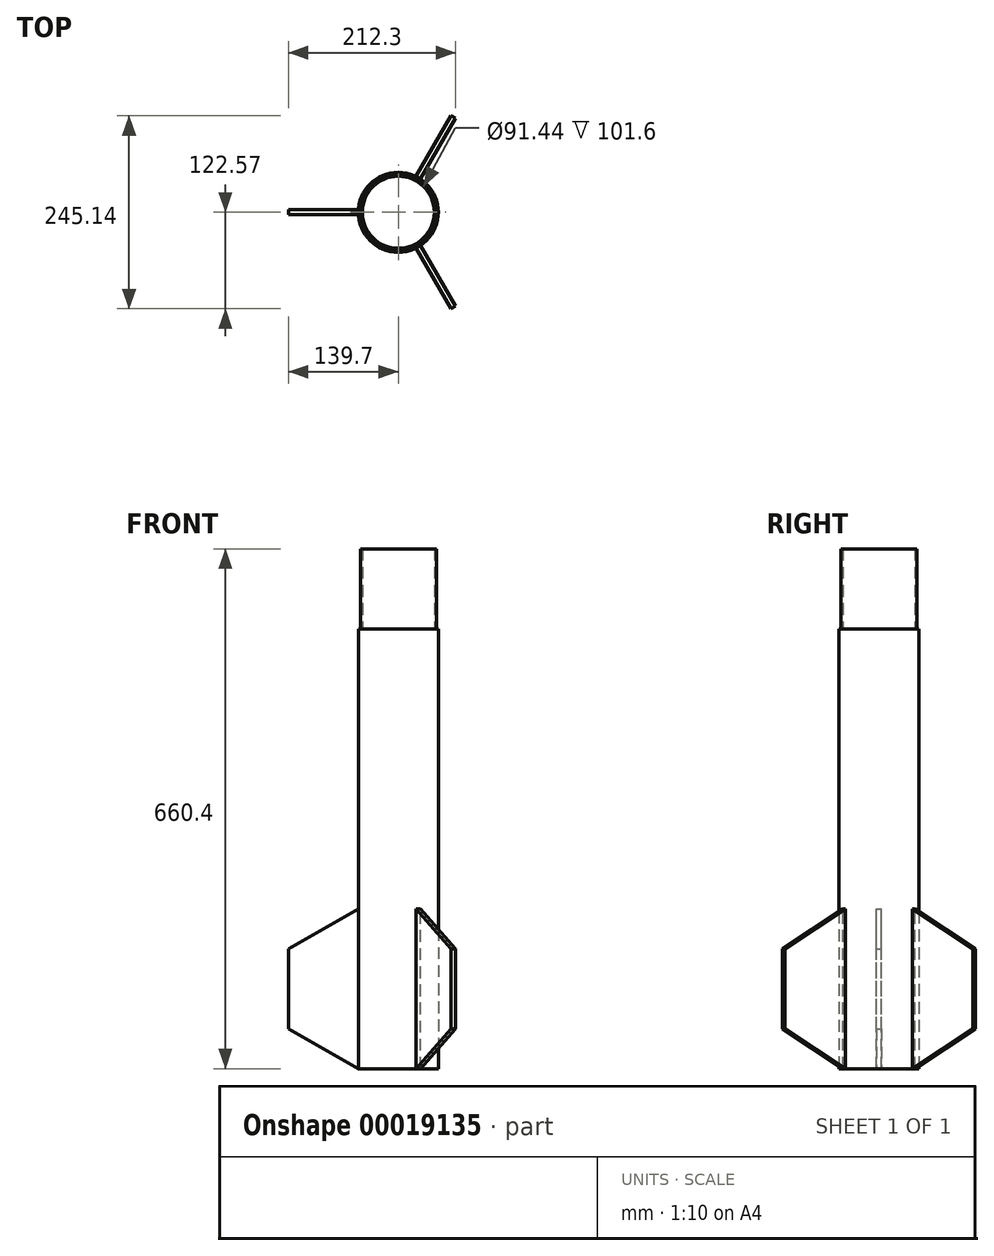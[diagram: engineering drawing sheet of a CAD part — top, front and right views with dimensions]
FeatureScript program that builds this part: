
annotation { "Feature Type Name" : "Feature", "Feature Type Description" : "" }
export const myFeature = defineFeature(function(context is Context, id is Id, definition is map)
    precondition{}
    {
        {
            var Q0;
            Q0=qCreatedBy(makeId("Top.planeOp"),FACE);
            var sketch = newSketch(context, id + "F0", { "sketchPlane" : qUnion([Q0])});
            skCircle(sketch, "E0", {"center": v(0, 0) * mm, "radius": 50.8 * mm});
            skSolve(sketch);
        }
        {
            var Q0;
            Q0=makeQuery(id+"F0.imprint","IMPRINT",FACE,{"disambiguationData":[TD([[makeQuery(id+"F0.imprint","IMPRINT",EDGE,{"derivedFrom":sQuery(id+"F0.wireOp",EDGE,"E0")}),1.0]])]});
            extrude(context, id + "F1", {"entities" : qUnion([Q0]), "depth" : 558.8 * mm});
        }
        {
            var Q0;
            Q0=qCreatedBy(makeId("Front.planeOp"),FACE);
            var sketch = newSketch(context, id + "F2", { "sketchPlane" : qUnion([Q0])});
            skLineSegment(sketch, "E1", {"start": v(-139.7, 50.8) * mm, "end": v(-139.7, 152.4) * mm});
            skLineSegment(sketch, "E2", {"start": v(-139.7, 152.4) * mm, "end": v(-50.8, 203.2) * mm});
            skLineSegment(sketch, "E3", {"start": v(-50.8, 0) * mm, "end": v(-50.8, 1676.4) * mm});
            skLineSegment(sketch, "E4", {"start": v(50.8, 1676.4) * mm, "end": v(50.8, 0) * mm});
            skLineSegment(sketch, "E5.0", {"start": v(-50.8, 0) * mm, "end": v(50.8, 0) * mm});
            skLineSegment(sketch, "E6", {"start": v(-139.7, 50.8) * mm, "end": v(-50.8, 0) * mm});
            skSolve(sketch);
        }
        {
            var Q0;
            Q0 = qSketchRegion(id + "F2", true);
            extrude(context, id + "F3", {"entities" : qUnion([Q0]), "endBound" : BoundingType.SYMMETRIC, "depth" : 6.35 * mm});
        }
        {
            var Q0;
            Q0=makeQuery(id+"F3.opExtrude","SWEPT_BODY",BODY,{"disambiguationData":[OSD([sQuery(id+"F2.wireOp",EDGE,"E1"),sQuery(id+"F2.wireOp",EDGE,"E2"),sQuery(id+"F2.wireOp",EDGE,"E3"),sQuery(id+"F2.wireOp",EDGE,"E6")])]});
            var Q1;
            Q1=makeQuery(id+"F1.opExtrude","SWEPT_FACE",FACE,{"disambiguationData":[OSD([sQuery(id+"F0.wireOp",EDGE,"E0")])]});
            circularPattern(context, id + "F4", {"entities" : qUnion([Q0]), "axis" : qUnion([Q1]), "angle" : 360 * degree, "instanceCount" : 3, "equalSpace" : true});
        }
        {
            var Q0;
            Q0=makeQuery(id+"F1.opExtrude","CAP_FACE",FACE,{"disambiguationData":[OSD([sQuery(id+"F0.wireOp",EDGE,"E0")])],"isStart":false});
            var sketch = newSketch(context, id + "F5", { "sketchPlane" : qUnion([Q0])});
            skCircle(sketch, "E7", {"center": v(0, 0) * mm, "radius": 48.26 * mm});
            skCircle(sketch, "E8", {"center": v(0, 0) * mm, "radius": 45.72 * mm});
            skSolve(sketch);
        }
        {
            var Q0;
            Q0=makeQuery(id+"F5.imprint","IMPRINT",FACE,{"disambiguationData":[TD([[makeQuery(id+"F5.imprint","IMPRINT",EDGE,{"derivedFrom":sQuery(id+"F5.wireOp",EDGE,"E7")}),1.0]])]});
            extrude(context, id + "F6", {"entities" : qUnion([Q0]), "operationType" : NewBodyOperationType.ADD, "depth" : 101.6 * mm});
        }
    });
